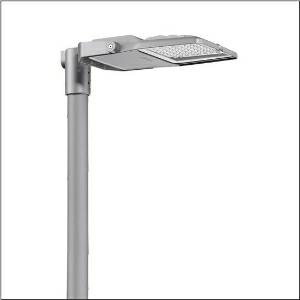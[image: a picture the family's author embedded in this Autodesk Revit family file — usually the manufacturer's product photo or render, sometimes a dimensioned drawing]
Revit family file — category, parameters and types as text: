
# Revit family: floodlight_fl_21_mini___pl64_5xa7772c2e3a_fee6
name_source: partatom
category: Lighting Fixtures
units: mm (PartAtom-declared; Revit-internal decimal feet)

## family parameters
Cut with Voids When Loaded = No
Host = Face
Light Source = No
Part Type = Normal
Room Calculation Point = No
Round Connector Dimension = Use Diameter
Shared = No

## types (1)
- --- (1 x LED, 11790 lm, 87.2 W, 3000K)
    Apparent Load = 87 VA
    CIE Flux Codes = 28 80 98 100 100
    Color Rendering = 70
    Color Temperature = 3000K
    Default Elevation = 1800 mm
    Description = Floodlight FL 21 mini, floodlight, primary light control with lens, of PMMA, primary optical cover: protective disc, of toughened safety glass, transparent, light distribution: PL64, light emission: direct distribution, installation type: surface-mounted, LED, High Power LED, rated luminous flux: 11.790lm, luminous efficacy: 135lm/W, light colour: 730, colour temperature: 3000K, control gear: ECG iQ, control: Auto-Match, Temp-Guard, Night-Set, Smart-Wire, Desk-Remote (wireless, voltage-free reading and setting of iQ features in the workshop via application-optimized NFC function/RFID function), optimised constant luminous flux control (CLO 2.0), Light-Fading, Lumen-Switch, with terminal, 6-pole, mains connection: 220..240V, AC, 50/60Hz, start of lifetime: 87W, end of lifetime: 92W, reduction: 40W, luminaire housing, of diecast aluminium, powder-coated, Siteco® metallic grey (DB 702S), corrosivity category C5 according to DIN EN ISO 12944, mast bracket, of steel, galvanised, powder-coated, protection rating (complete): IP66, insulation class (complete): insulation class II (safety insulation), certification: CE, ENEC, VDE, protection symbol: D, impact resistance: IK08, permissible operating ambient temperature: -40..+40°C, permissible operating ambient temperature for outdoor applications: -40..+50°C, standard: DIN EN 12944, packaging unit: 1 piece

Light Distribution: PL64
    Height = 70 mm
    Lamp = 1 x LED
    Lamp Light Flux = 11790 lm
    Lamp Power = 87.2 W
    Lamp count = 1
    Length = 485 mm
    Luminous efficacy = 135 lm/W
    Manufacturer = Siteco
    ModVariant = No
    Model = 5XA7772C2E3A
    Number of Poles = 1
    OnlyDefault = Yes
    Power Factor = 1
    Product Name = Floodlight FL 21 mini | PL64
    Product group = floodlight | pylon top
    ProductGroupID = 6101
    Protection Class = Protection class II
    Protection Degree = IP 66
    RLX_Detail_Level = 1
    RlxData = <blob elided: 101217 chars, md5=f6e278e5>
    Socket = socket
    Standby Power = 0 W
    System Light Flux = 11790 lm
    System Power = 87 W
    Type Comments = factory setting: luminous flux: 100 % | dim-lin: 254 | 456 mA
    Type Image = l_1007125.jpg
    URL = http://relux.com
    VarID = @adj_077413
    Voltage = 0 V
    Weight = 0.00 kg
    Width = 337 mm

## geometry (parser evidence)
native form markers: Blend x4, Sweep x11
no freeform markers — native parametric forms only
